# Revit family: Diffuser-Carnes-SPJB-Square_Neck
name_source: partatom
category: Duct Accessories
revit_build: Autodesk Revit Architecture 2012 (Build: 20110309_2315(x64)
units: mm (PartAtom-declared; Revit-internal decimal feet)

## types (9) — shared parameters
Catalog = http://www.carnes.com
Description = Perforated Diffusers
Diffuser Plate = Metal - Carnes - Plate - Mesh
Flow = 0 CFM
Manufacturer = CARNES COMPANY
Model = SPJB
Panel Options = http://www.carnes.com
Product Page URL = http://www.carnes.com
Return Connection = Diffuser Return Connector
Return Connector = Yes
Specification Sheet = http://www.carnes.com
Square & Rectangular Neck = http://www.carnes.com
Subcatagory = Air Distribution
URL = http://www.carnes.com
Unit = Metal - Carnes - Steel Galvanized
zero-valued in all types: Default Elevation

## per-type parameters (varying)
| type | Diffuser Width B | Height C | Width A |
| SPJB114 6x6 | 6" | 3.25 " | 11.75 " |
| SPJB114 6x8 | 8" | 3.25 " | 11.75 " |
| SPJB224 6x6 | 6" | 3.5 " | 23.75 " |
| SPJB224 8x8 | 8" | 3.5 " | 23.75 " |
| SPJB224 10x10 | 10" | 3.5 " | 23.75 " |
| SPJB224 12x12 | 12" | 3.5 " | 23.75 " |
| SPJB224 14x14 | 14" | 3.5 " | 23.75 " |
| SPJB224 16x16 | 16" | 3.5 " | 23.75 " |
| SPJB224 18x18 | 18" | 3.5 " | 23.75 " |

## geometry (parser evidence)
native form markers: Blend x9, Sweep x2
no freeform markers — native parametric forms only
